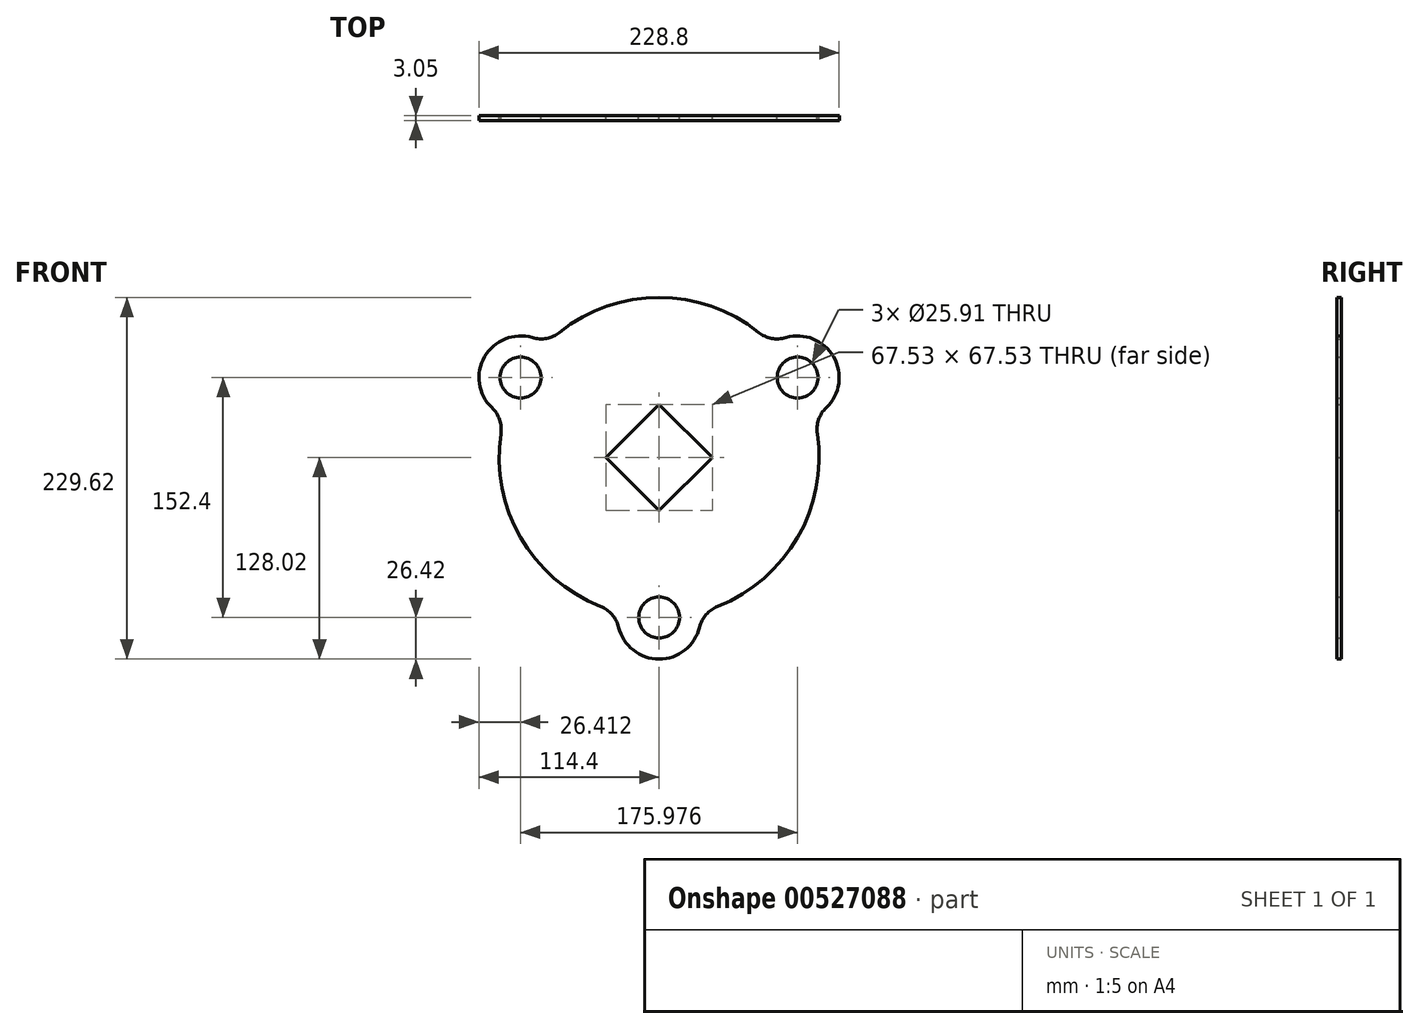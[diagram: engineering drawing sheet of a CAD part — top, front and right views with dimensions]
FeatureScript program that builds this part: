
annotation { "Feature Type Name" : "Feature", "Feature Type Description" : "" }
export const myFeature = defineFeature(function(context is Context, id is Id, definition is map)
    precondition{}
    {
        {
            var Q0;
            Q0=qCreatedBy(makeId("Front.planeOp"),FACE);
            var sketch = newSketch(context, id + "F0", { "sketchPlane" : qUnion([Q0])});
            skLineSegment(sketch, "E0", {"start": v(-101.6, 0) * mm, "end": v(101.6, 0) * mm, "construction": true});
            skPoint(sketch, "E1", {"position": v(0, 0) * mm});
            skLineSegment(sketch, "E2", {"start": v(0, 101.6) * mm, "end": v(0, -101.6) * mm, "construction": true});
            skLineSegment(sketch, "E3", {"start": v(0, 0) * mm, "end": v(87.99, 50.8) * mm, "construction": true});
            skArc(sketch, "E4", {"start": v(-100.48, 15.04) * mm, "mid": v(-87.99, -50.8) * mm, "end": v(-37.22, -94.54) * mm});
            skLineSegment(sketch, "E5", {"start": v(0, 33.77) * mm, "end": v(33.77, 0) * mm});
            skLineSegment(sketch, "E6", {"start": v(33.77, 0) * mm, "end": v(0, -33.77) * mm});
            skLineSegment(sketch, "E7", {"start": v(0, -33.77) * mm, "end": v(-33.77, 0) * mm});
            skLineSegment(sketch, "E8", {"start": v(-33.77, 0) * mm, "end": v(0, 33.77) * mm});
            skCircle(sketch, "E9", {"center": v(87.99, 50.8) * mm, "radius": 12.95 * mm});
            skCircle(sketch, "E10.1.0", {"center": v(-87.99, 50.8) * mm, "radius": 12.95 * mm});
            skCircle(sketch, "E10.2.0", {"center": v(0, -101.6) * mm, "radius": 12.95 * mm});
            skArc(sketch, "E11", {"start": v(106.2, 31.66) * mm, "mid": v(110.87, 64) * mm, "end": v(80.51, 76.14) * mm});
            skArc(sketch, "E12.1.0", {"start": v(-80.51, 76.14) * mm, "mid": v(-110.87, 64) * mm, "end": v(-106.2, 31.66) * mm});
            skArc(sketch, "E12.2.0", {"start": v(-25.68, -107.8) * mm, "mid": v(0, -128.02) * mm, "end": v(25.68, -107.8) * mm});
            skArc(sketch, "E13.trimOffspring", {"start": v(63.26, 79.5) * mm, "mid": v(0, 101.6) * mm, "end": v(-63.26, 79.5) * mm});
            skArc(sketch, "E14.trimOffspring", {"start": v(37.22, -94.54) * mm, "mid": v(87.99, -50.8) * mm, "end": v(100.48, 15.04) * mm});
            skPoint(sketch, "E15.visualSharp", {"position": v(-71.92, 71.77) * mm});
            skArc(sketch, "E15.filletArc", {"start": v(-80.51, 76.14) * mm, "mid": v(-71.48, 75.71) * mm, "end": v(-63.26, 79.5) * mm});
            skPoint(sketch, "E16.visualSharp", {"position": v(-98.11, 26.4) * mm});
            skArc(sketch, "E16.filletArc", {"start": v(-100.48, 15.04) * mm, "mid": v(-101.3, 24.05) * mm, "end": v(-106.2, 31.66) * mm});
            skPoint(sketch, "E17.visualSharp", {"position": v(-26.2, -98.17) * mm});
            skArc(sketch, "E17.filletArc", {"start": v(-25.68, -107.8) * mm, "mid": v(-29.83, -99.76) * mm, "end": v(-37.22, -94.54) * mm});
            skPoint(sketch, "E18.visualSharp", {"position": v(26.2, -98.17) * mm});
            skArc(sketch, "E18.filletArc", {"start": v(37.22, -94.54) * mm, "mid": v(29.83, -99.76) * mm, "end": v(25.68, -107.8) * mm});
            skPoint(sketch, "E19.visualSharp", {"position": v(98.11, 26.4) * mm});
            skArc(sketch, "E19.filletArc", {"start": v(106.2, 31.66) * mm, "mid": v(101.3, 24.05) * mm, "end": v(100.48, 15.04) * mm});
            skPoint(sketch, "E20.visualSharp", {"position": v(71.92, 71.77) * mm});
            skArc(sketch, "E20.filletArc", {"start": v(63.26, 79.5) * mm, "mid": v(71.48, 75.71) * mm, "end": v(80.51, 76.14) * mm});
            skSolve(sketch);
        }
        {
            var Q0;
            Q0 = qSketchRegion(id + "F0", true);
            extrude(context, id + "F1", {"entities" : qUnion([Q0]), "depth" : 3.05 * mm, "offsetDistance" : 25.4 * mm});
        }
    });
